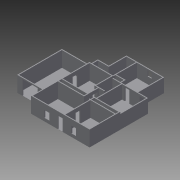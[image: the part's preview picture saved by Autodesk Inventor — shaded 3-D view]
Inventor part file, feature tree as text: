
AUTODESK INVENTOR PART (.ipt)
format: ipt  version: 2013 SP2 (Build 170200200, 200)  size: 536,064 bytes
history: native  units: in
note: dims shown in document units (in); Inventor stores cm internally (conversion verified against a paired STEP export)
features: extrude x11, sketch x7, projected_geometry x3
ambient origin geometry x8: Origin, YZ Plane, XZ Plane, XY Plane, X Axis, Y Axis, Z Axis, Center Point
bodies: Solid1 (feature_tree)
feature tree (21):
  extrude  "Extrusion1"  Depth=66.0in
  extrude  "Extrusion2"  Depth=168.0in
  extrude  "Extrusion3"  Depth=6.0in
  extrude  "Extrusion4"  Depth=6.0in
  extrude  "Extrusion5"  Depth=73.0in
  sketch  "Sketch6"  dims[d18=6.0in d19=171.0in d20=73.0in]
  extrude  "Extrusion6"  Depth=6.0in
  extrude  "Extrusion7"  Depth=174.0in
  extrude  "Extrusion8"  Depth=180.0in
  extrude  "Extrusion9"  Depth=6.0in
  extrude  "Extrusion10"  Depth=6.0in
  extrude  "Extrusion11"  Depth=6.0in
  sketch  "Sketch2"  dims[d0=392.0in d3=66.0in]
  projected_geometry  "Projected Loop1"
  sketch  "Sketch3"  dims[d4=174.0in d5=74.0in d8=168.0in d9=300.0in d10=75.0in]
  sketch  "Sketch4"  dims[d11=392.0in d13=6.0in d14=6.0in]
  sketch  "Sketch5"  dims[d15=6.0in d16=6.0in d17=6.0in]
  projected_geometry  "Projected Loop2"
  projected_geometry  "Projected Loop3"
  sketch  "Sketch7"  dims[d21=253.0in d22=6.0in]
  sketch  "Sketch8"  dims[d23=6.0in d24=174.0in d25=180.0in d27=6.0in d28=6.0in d30=6.0in d31=36.0in d32=138.0in d33=6.0in d34=300.0in d35=75.0in d36=6.0in d37=212.0in d38=392.0in d39=6.0in d40=75.0in d41=392.0in d42=6.0in d43=6.0in d44=6.0in d45=166.0in d46=6.0in d47=168.0in d48=6.0in d50=6.0in d53=142.0in d54=174.0in d56=43.0in d57=43.0in d58=6.0in d59=162.0in d60=6.0in d62=6.0in d63=114.0in d64=141.0in d65=6.0in d66=6.0in d67=6.0in d69=6.0in d71=208.0in d72=141.0in d73=6.0in d74=181.0in d76=22.0in d79=6.0in d81=138.0in d83=64.0in d84=113.0in d85=145.0in d86=6.0in d87=181.0in d88=168.0in d89=34.0in d90=31.0in d91=114.0in d92=114.0in d93=176.0in d94=6.0in d95=180.0in d96=180.0in d97=162.0in d98=31.0in d99=6.0in d100=6.0in d101=175.0in d103=66.0in d104=99.0in d105=168.0in d106=6.0in d107=73.0in d108=69.0in d109=100.0in d110=212.0in d111=212.0in d112=144.0in d113=25.0in d114=6.0in d115=138.0in d116=6.0in d117=171.0in d119=6.0in d120=6.0in d121=6.0in d122=108.0in d123=90.0in d124=0.0in d125=1.0in d126=0.0in d127=25.0in d128=20.0in d129=25.0in d130=20.0in d131=90.0in d132=122.0in d133=90.0in d134=122.0in d135=1.0in d136=0.0in d137=12.0in d138=22.0in d139=15.0in d140=22.0in d141=1.0in d142=0.0in d143=8.0in d144=47.0in d145=78.0in d146=105.0in d147=1.0in d148=0.0in d149=12.0in d150=0.0in d151=11.0in d152=0.0in d153=10.0in d154=0.0in d155=8.0in d156=0.0in d157=13.0in d158=0.0in d159=8.0in d160=0.0in d161=32.0in]
